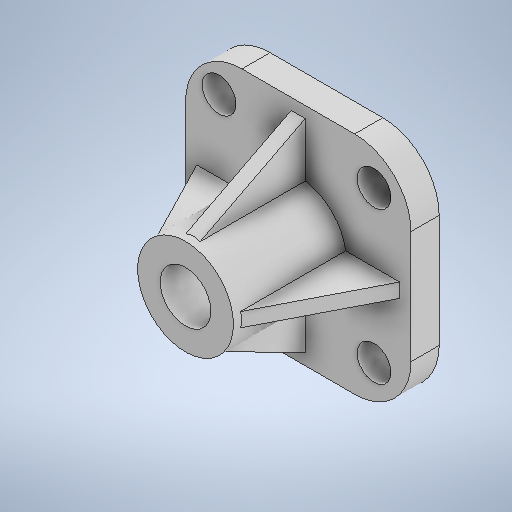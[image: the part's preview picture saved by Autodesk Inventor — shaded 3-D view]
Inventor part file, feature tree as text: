
AUTODESK INVENTOR PART (.ipt)
format: ipt  version: 2025.2 (Build 292293000, 293)  size: 637,952 bytes
history: native  units: in
note: dims shown in document units (in); Inventor stores cm internally (conversion verified against a paired STEP export)
features: sketch x4, extrude x2, rib x1, pattern_circular x1, other x1
ambient origin geometry x8: Origin, YZ Plane, XZ Plane, XY Plane, X Axis, Y Axis, Z Axis, Center Point
bodies: Solid1 (feature_tree)
feature tree (9):
  extrude  "Extrusion1"  Depth=3.1496in
  extrude  "Extrusion2"  Depth=0.7874in
  sketch  "Sketch3"  dims[d11=0.4724in]
  rib  "Rib1"
  pattern_circular  "Circular Pattern1"  [2 undecoded]
  sketch  "Sketch1"  dims[d5=3.1496in d6=3.1496in]
  other  "Image1"
  sketch  "Sketch2"  dims[d7=0.7874in d9=0.4724in]
  sketch  "Sketch4"  dims[d12=2.1654in d14=0.3937in d15=0.0in d16=1.3386in d17=0.7087in d18=1.5748in d19=0.0in d22=0.0394in d23=0.1969in d24=0.0in d25=0.0in d26=0.0394in d27=0.0394in d28=1.5748in d29=360.0deg]
note: 2 required parameter values undecoded (feature->parameter linkage not recoverable at this tier; creation-order binding heuristic only, values carry confidence <= 0.55)
